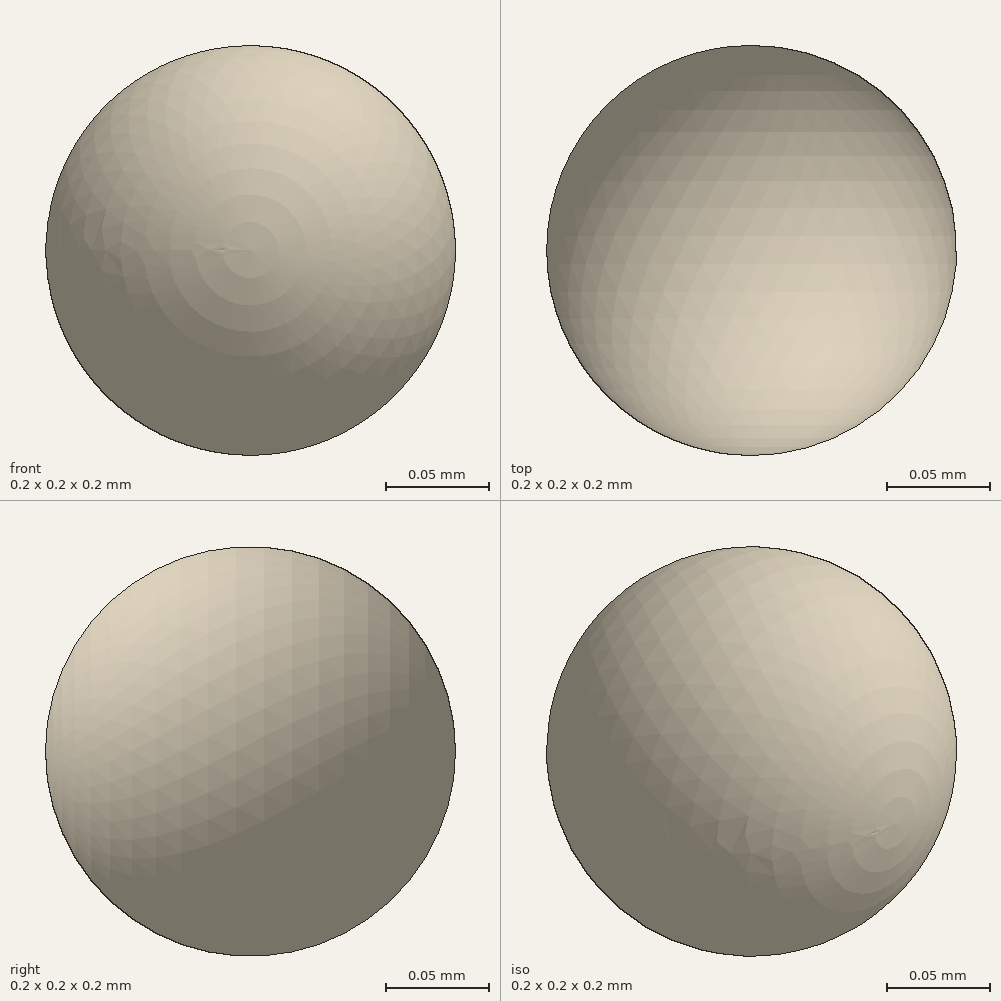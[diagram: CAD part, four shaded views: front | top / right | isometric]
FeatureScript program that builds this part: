
annotation { "Feature Type Name" : "Feature", "Feature Type Description" : "" }
export const myFeature = defineFeature(function(context is Context, id is Id, definition is map)
    precondition{}
    {
        {
            var Q0;
            Q0=qCreatedBy(makeId("Top.planeOp"),FACE);
            var sketch = newSketch(context, id + "F0", { "sketchPlane" : qUnion([Q0])});
            skArc(sketch, "E0", {"start": v(0, -0.1) * mm, "mid": v(0.1, 0) * mm, "end": v(0, 0.1) * mm});
            skLineSegment(sketch, "E1", {"start": v(0, 0.1) * mm, "end": v(0, -0.1) * mm});
            skLineSegment(sketch, "E2", {"start": v(0, 1.67) * mm, "end": v(0, -1.8) * mm, "construction": true});
            skSolve(sketch);
        }
        {
            var Q0;
            Q0=qSketchRegion(id+"F0",true);
            var Q1;
            Q1=sQuery(id+"F0.wireOp",EDGE,"E2");
            revolve(context, id + "F1", {"entities" : qUnion([Q0]), "axis" : qUnion([Q1]), "revolveType" : RevolveType.FULL});
        }
    });
